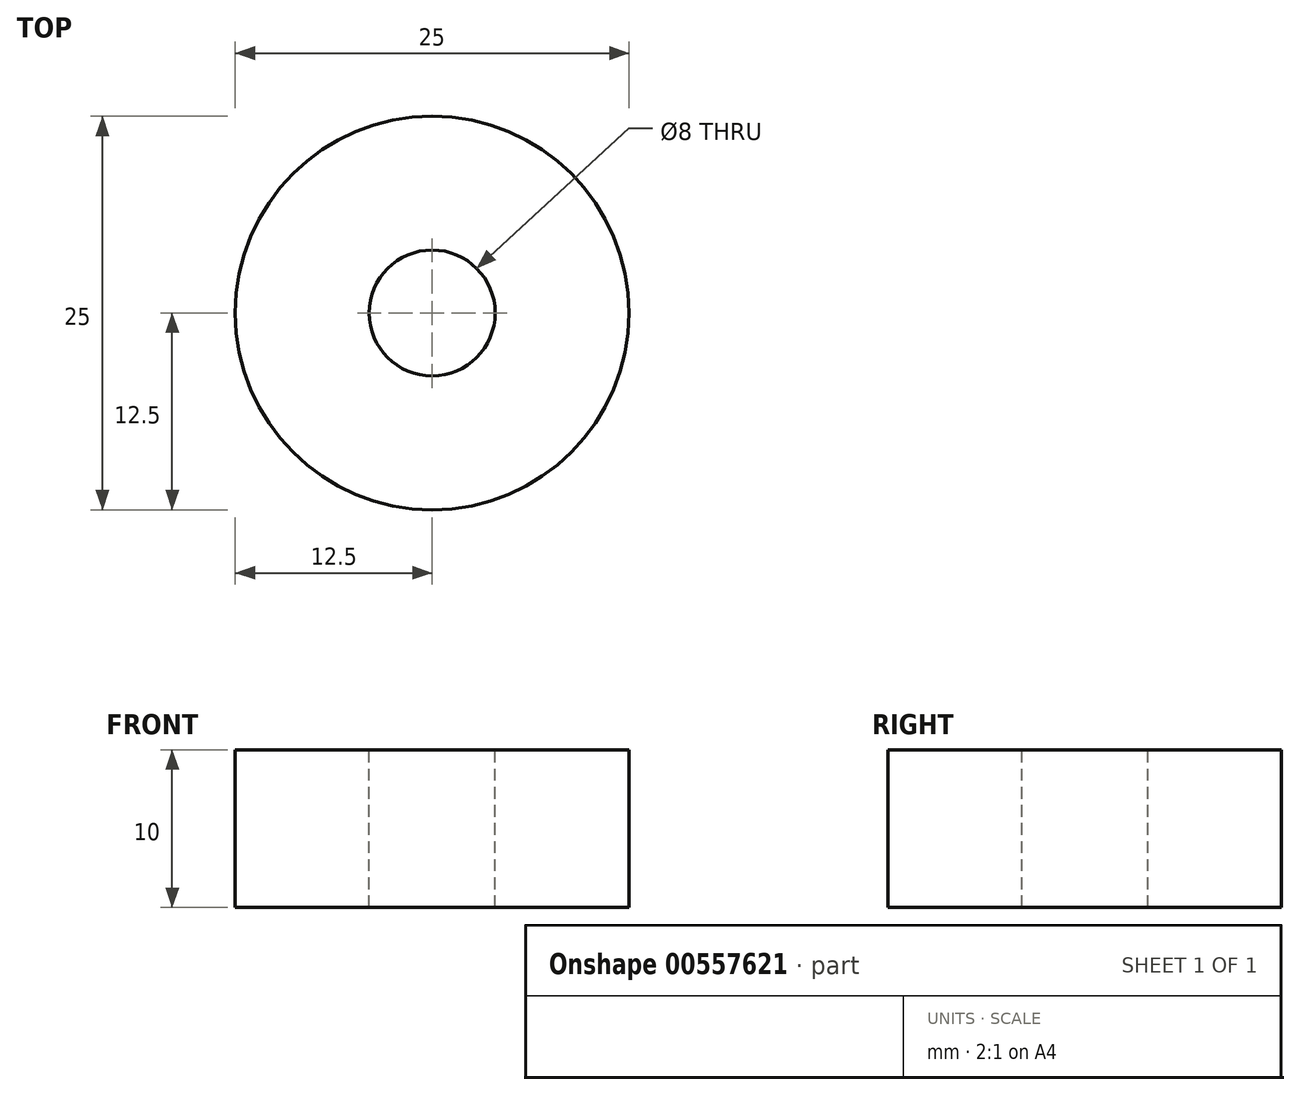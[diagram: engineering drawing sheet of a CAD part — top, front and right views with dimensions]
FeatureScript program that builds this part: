
annotation { "Feature Type Name" : "Feature", "Feature Type Description" : "" }
export const myFeature = defineFeature(function(context is Context, id is Id, definition is map)
    precondition{}
    {
        {
            var Q0;
            Q0=qCreatedBy(makeId("Top.planeOp"),FACE);
            var sketch = newSketch(context, id + "F0", { "sketchPlane" : qUnion([Q0])});
            skCircle(sketch, "E0", {"center": v(0, 0) * mm, "radius": 4 * mm});
            skCircle(sketch, "E1", {"center": v(0, 0) * mm, "radius": 4.5 * mm});
            skCircle(sketch, "E2", {"center": v(0, 0) * mm, "radius": 5.5 * mm});
            skCircle(sketch, "E3", {"center": v(0, 0) * mm, "radius": 6.5 * mm});
            skCircle(sketch, "E4", {"center": v(0, 0) * mm, "radius": 8 * mm});
            skCircle(sketch, "E5", {"center": v(0, 0) * mm, "radius": 9 * mm});
            skCircle(sketch, "E6", {"center": v(0, 0) * mm, "radius": 10.5 * mm});
            skCircle(sketch, "E7", {"center": v(0, 0) * mm, "radius": 12.5 * mm});
            skLineSegment(sketch, "E8", {"start": v(0, 0) * mm, "end": v(-12.5, 0) * mm});
            skLineSegment(sketch, "E9", {"start": v(0, 0) * mm, "end": v(0, -12.5) * mm});
            skLineSegment(sketch, "E10", {"start": v(0, 0) * mm, "end": v(8.84, 8.84) * mm});
            skSolve(sketch);
        }
        {
            var Q0;
            {var subQ0=sQuery(id+"F0.wireOp",EDGE,"E10");var subQ1=sQuery(id+"F0.wireOp",EDGE,"E1");var subQ2=makeQuery(id+"F0.imprint","INTERSECT",VERTEX,{"derivedFrom":[subQ1,subQ0]});Q0=makeQuery(id+"F0.imprint","IMPRINT",FACE,{"disambiguationData":[TD([[makeQuery(id+"F0.imprint","IMPRINT",EDGE,{"disambiguationData":[TD([[subQ2,1.0]])],"derivedFrom":subQ1}),-1.0]])]});}
            var Q1;
            {var subQ0=sQuery(id+"F0.wireOp",EDGE,"E10");var subQ1=sQuery(id+"F0.wireOp",EDGE,"E2");var subQ2=makeQuery(id+"F0.imprint","INTERSECT",VERTEX,{"derivedFrom":[subQ1,subQ0]});Q1=makeQuery(id+"F0.imprint","IMPRINT",FACE,{"disambiguationData":[TD([[makeQuery(id+"F0.imprint","IMPRINT",EDGE,{"disambiguationData":[TD([[subQ2,1.0]])],"derivedFrom":subQ1}),-1.0]])]});}
            var Q2;
            {var subQ0=sQuery(id+"F0.wireOp",EDGE,"E10");var subQ1=sQuery(id+"F0.wireOp",EDGE,"E3");var subQ2=makeQuery(id+"F0.imprint","INTERSECT",VERTEX,{"derivedFrom":[subQ1,subQ0]});Q2=makeQuery(id+"F0.imprint","IMPRINT",FACE,{"disambiguationData":[TD([[makeQuery(id+"F0.imprint","IMPRINT",EDGE,{"disambiguationData":[TD([[subQ2,1.0]])],"derivedFrom":subQ1}),-1.0]])]});}
            var Q3;
            {var subQ0=sQuery(id+"F0.wireOp",EDGE,"E10");var subQ1=sQuery(id+"F0.wireOp",EDGE,"E4");var subQ2=makeQuery(id+"F0.imprint","INTERSECT",VERTEX,{"derivedFrom":[subQ1,subQ0]});Q3=makeQuery(id+"F0.imprint","IMPRINT",FACE,{"disambiguationData":[TD([[makeQuery(id+"F0.imprint","IMPRINT",EDGE,{"disambiguationData":[TD([[subQ2,1.0]])],"derivedFrom":subQ1}),-1.0]])]});}
            var Q4;
            {var subQ0=sQuery(id+"F0.wireOp",EDGE,"E10");var subQ1=sQuery(id+"F0.wireOp",EDGE,"E6");var subQ2=makeQuery(id+"F0.imprint","INTERSECT",VERTEX,{"derivedFrom":[subQ1,subQ0]});Q4=makeQuery(id+"F0.imprint","IMPRINT",FACE,{"disambiguationData":[TD([[makeQuery(id+"F0.imprint","IMPRINT",EDGE,{"disambiguationData":[TD([[subQ2,1.0]])],"derivedFrom":subQ1}),-1.0]])]});}
            var Q5;
            {var subQ0=sQuery(id+"F0.wireOp",EDGE,"E8");var subQ1=sQuery(id+"F0.wireOp",EDGE,"E6");var subQ2=makeQuery(id+"F0.imprint","INTERSECT",VERTEX,{"derivedFrom":[subQ1,subQ0]});Q5=makeQuery(id+"F0.imprint","IMPRINT",FACE,{"disambiguationData":[TD([[makeQuery(id+"F0.imprint","IMPRINT",EDGE,{"disambiguationData":[TD([[subQ2,1.0]])],"derivedFrom":subQ1}),-1.0]])]});}
            var Q6;
            {var subQ0=sQuery(id+"F0.wireOp",EDGE,"E8");var subQ1=sQuery(id+"F0.wireOp",EDGE,"E5");var subQ2=makeQuery(id+"F0.imprint","INTERSECT",VERTEX,{"derivedFrom":[subQ1,subQ0]});Q6=makeQuery(id+"F0.imprint","IMPRINT",FACE,{"disambiguationData":[TD([[makeQuery(id+"F0.imprint","IMPRINT",EDGE,{"disambiguationData":[TD([[subQ2,1.0]])],"derivedFrom":subQ1}),-1.0]])]});}
            var Q7;
            {var subQ0=sQuery(id+"F0.wireOp",EDGE,"E8");var subQ1=sQuery(id+"F0.wireOp",EDGE,"E4");var subQ2=makeQuery(id+"F0.imprint","INTERSECT",VERTEX,{"derivedFrom":[subQ1,subQ0]});Q7=makeQuery(id+"F0.imprint","IMPRINT",FACE,{"disambiguationData":[TD([[makeQuery(id+"F0.imprint","IMPRINT",EDGE,{"disambiguationData":[TD([[subQ2,1.0]])],"derivedFrom":subQ1}),-1.0]])]});}
            var Q8;
            {var subQ0=sQuery(id+"F0.wireOp",EDGE,"E8");var subQ1=sQuery(id+"F0.wireOp",EDGE,"E3");var subQ2=makeQuery(id+"F0.imprint","INTERSECT",VERTEX,{"derivedFrom":[subQ1,subQ0]});Q8=makeQuery(id+"F0.imprint","IMPRINT",FACE,{"disambiguationData":[TD([[makeQuery(id+"F0.imprint","IMPRINT",EDGE,{"disambiguationData":[TD([[subQ2,1.0]])],"derivedFrom":subQ1}),-1.0]])]});}
            var Q9;
            {var subQ0=sQuery(id+"F0.wireOp",EDGE,"E10");var subQ1=sQuery(id+"F0.wireOp",EDGE,"E5");var subQ2=makeQuery(id+"F0.imprint","INTERSECT",VERTEX,{"derivedFrom":[subQ1,subQ0]});Q9=makeQuery(id+"F0.imprint","IMPRINT",FACE,{"disambiguationData":[TD([[makeQuery(id+"F0.imprint","IMPRINT",EDGE,{"disambiguationData":[TD([[subQ2,1.0]])],"derivedFrom":subQ1}),-1.0]])]});}
            var Q10;
            {var subQ0=sQuery(id+"F0.wireOp",EDGE,"E8");var subQ1=sQuery(id+"F0.wireOp",EDGE,"E1");var subQ2=makeQuery(id+"F0.imprint","INTERSECT",VERTEX,{"derivedFrom":[subQ1,subQ0]});Q10=makeQuery(id+"F0.imprint","IMPRINT",FACE,{"disambiguationData":[TD([[makeQuery(id+"F0.imprint","IMPRINT",EDGE,{"disambiguationData":[TD([[subQ2,1.0]])],"derivedFrom":subQ1}),-1.0]])]});}
            var Q11;
            {var subQ0=sQuery(id+"F0.wireOp",EDGE,"E8");var subQ1=sQuery(id+"F0.wireOp",EDGE,"E2");var subQ2=makeQuery(id+"F0.imprint","INTERSECT",VERTEX,{"derivedFrom":[subQ1,subQ0]});Q11=makeQuery(id+"F0.imprint","IMPRINT",FACE,{"disambiguationData":[TD([[makeQuery(id+"F0.imprint","IMPRINT",EDGE,{"disambiguationData":[TD([[subQ2,1.0]])],"derivedFrom":subQ1}),-1.0]])]});}
            var Q12;
            {var subQ0=sQuery(id+"F0.wireOp",EDGE,"E10");var subQ1=sQuery(id+"F0.wireOp",EDGE,"E0");var subQ2=makeQuery(id+"F0.imprint","INTERSECT",VERTEX,{"derivedFrom":[subQ1,subQ0]});Q12=makeQuery(id+"F0.imprint","IMPRINT",FACE,{"disambiguationData":[TD([[makeQuery(id+"F0.imprint","IMPRINT",EDGE,{"disambiguationData":[TD([[subQ2,1.0]])],"derivedFrom":subQ1}),-1.0]])]});}
            var Q13;
            {var subQ0=sQuery(id+"F0.wireOp",EDGE,"E8");var subQ1=sQuery(id+"F0.wireOp",EDGE,"E0");var subQ2=makeQuery(id+"F0.imprint","INTERSECT",VERTEX,{"derivedFrom":[subQ1,subQ0]});Q13=makeQuery(id+"F0.imprint","IMPRINT",FACE,{"disambiguationData":[TD([[makeQuery(id+"F0.imprint","IMPRINT",EDGE,{"disambiguationData":[TD([[subQ2,1.0]])],"derivedFrom":subQ1}),-1.0]])]});}
            var Q14;
            {var subQ0=sQuery(id+"F0.wireOp",EDGE,"E8");var subQ1=sQuery(id+"F0.wireOp",EDGE,"E0");var subQ2=makeQuery(id+"F0.imprint","INTERSECT",VERTEX,{"derivedFrom":[subQ1,subQ0]});Q14=makeQuery(id+"F0.imprint","IMPRINT",FACE,{"disambiguationData":[TD([[makeQuery(id+"F0.imprint","IMPRINT",EDGE,{"disambiguationData":[TD([[subQ2,-1.0]])],"derivedFrom":subQ1}),-1.0]])]});}
            var Q15;
            {var subQ0=sQuery(id+"F0.wireOp",EDGE,"E8");var subQ1=sQuery(id+"F0.wireOp",EDGE,"E1");var subQ2=makeQuery(id+"F0.imprint","INTERSECT",VERTEX,{"derivedFrom":[subQ1,subQ0]});Q15=makeQuery(id+"F0.imprint","IMPRINT",FACE,{"disambiguationData":[TD([[makeQuery(id+"F0.imprint","IMPRINT",EDGE,{"disambiguationData":[TD([[subQ2,-1.0]])],"derivedFrom":subQ1}),-1.0]])]});}
            var Q16;
            {var subQ0=sQuery(id+"F0.wireOp",EDGE,"E8");var subQ1=sQuery(id+"F0.wireOp",EDGE,"E2");var subQ2=makeQuery(id+"F0.imprint","INTERSECT",VERTEX,{"derivedFrom":[subQ1,subQ0]});Q16=makeQuery(id+"F0.imprint","IMPRINT",FACE,{"disambiguationData":[TD([[makeQuery(id+"F0.imprint","IMPRINT",EDGE,{"disambiguationData":[TD([[subQ2,-1.0]])],"derivedFrom":subQ1}),-1.0]])]});}
            var Q17;
            {var subQ0=sQuery(id+"F0.wireOp",EDGE,"E8");var subQ1=sQuery(id+"F0.wireOp",EDGE,"E3");var subQ2=makeQuery(id+"F0.imprint","INTERSECT",VERTEX,{"derivedFrom":[subQ1,subQ0]});Q17=makeQuery(id+"F0.imprint","IMPRINT",FACE,{"disambiguationData":[TD([[makeQuery(id+"F0.imprint","IMPRINT",EDGE,{"disambiguationData":[TD([[subQ2,-1.0]])],"derivedFrom":subQ1}),-1.0]])]});}
            var Q18;
            {var subQ0=sQuery(id+"F0.wireOp",EDGE,"E8");var subQ1=sQuery(id+"F0.wireOp",EDGE,"E4");var subQ2=makeQuery(id+"F0.imprint","INTERSECT",VERTEX,{"derivedFrom":[subQ1,subQ0]});Q18=makeQuery(id+"F0.imprint","IMPRINT",FACE,{"disambiguationData":[TD([[makeQuery(id+"F0.imprint","IMPRINT",EDGE,{"disambiguationData":[TD([[subQ2,-1.0]])],"derivedFrom":subQ1}),-1.0]])]});}
            var Q19;
            {var subQ0=sQuery(id+"F0.wireOp",EDGE,"E8");var subQ1=sQuery(id+"F0.wireOp",EDGE,"E5");var subQ2=makeQuery(id+"F0.imprint","INTERSECT",VERTEX,{"derivedFrom":[subQ1,subQ0]});Q19=makeQuery(id+"F0.imprint","IMPRINT",FACE,{"disambiguationData":[TD([[makeQuery(id+"F0.imprint","IMPRINT",EDGE,{"disambiguationData":[TD([[subQ2,-1.0]])],"derivedFrom":subQ1}),-1.0]])]});}
            var Q20;
            {var subQ0=sQuery(id+"F0.wireOp",EDGE,"E8");var subQ1=sQuery(id+"F0.wireOp",EDGE,"E6");var subQ2=makeQuery(id+"F0.imprint","INTERSECT",VERTEX,{"derivedFrom":[subQ1,subQ0]});Q20=makeQuery(id+"F0.imprint","IMPRINT",FACE,{"disambiguationData":[TD([[makeQuery(id+"F0.imprint","IMPRINT",EDGE,{"disambiguationData":[TD([[subQ2,-1.0]])],"derivedFrom":subQ1}),-1.0]])]});}
            extrude(context, id + "F1", {"entities" : qUnion([Q0, Q1, Q2, Q3, Q4, Q5, Q6, Q7, Q8, Q9, Q10, Q11, Q12, Q13, Q14, Q15, Q16, Q17, Q18, Q19, Q20]), "oppositeDirection" : true, "depth" : 10 * mm, "offsetDistance" : 25 * mm});
        }
    });
